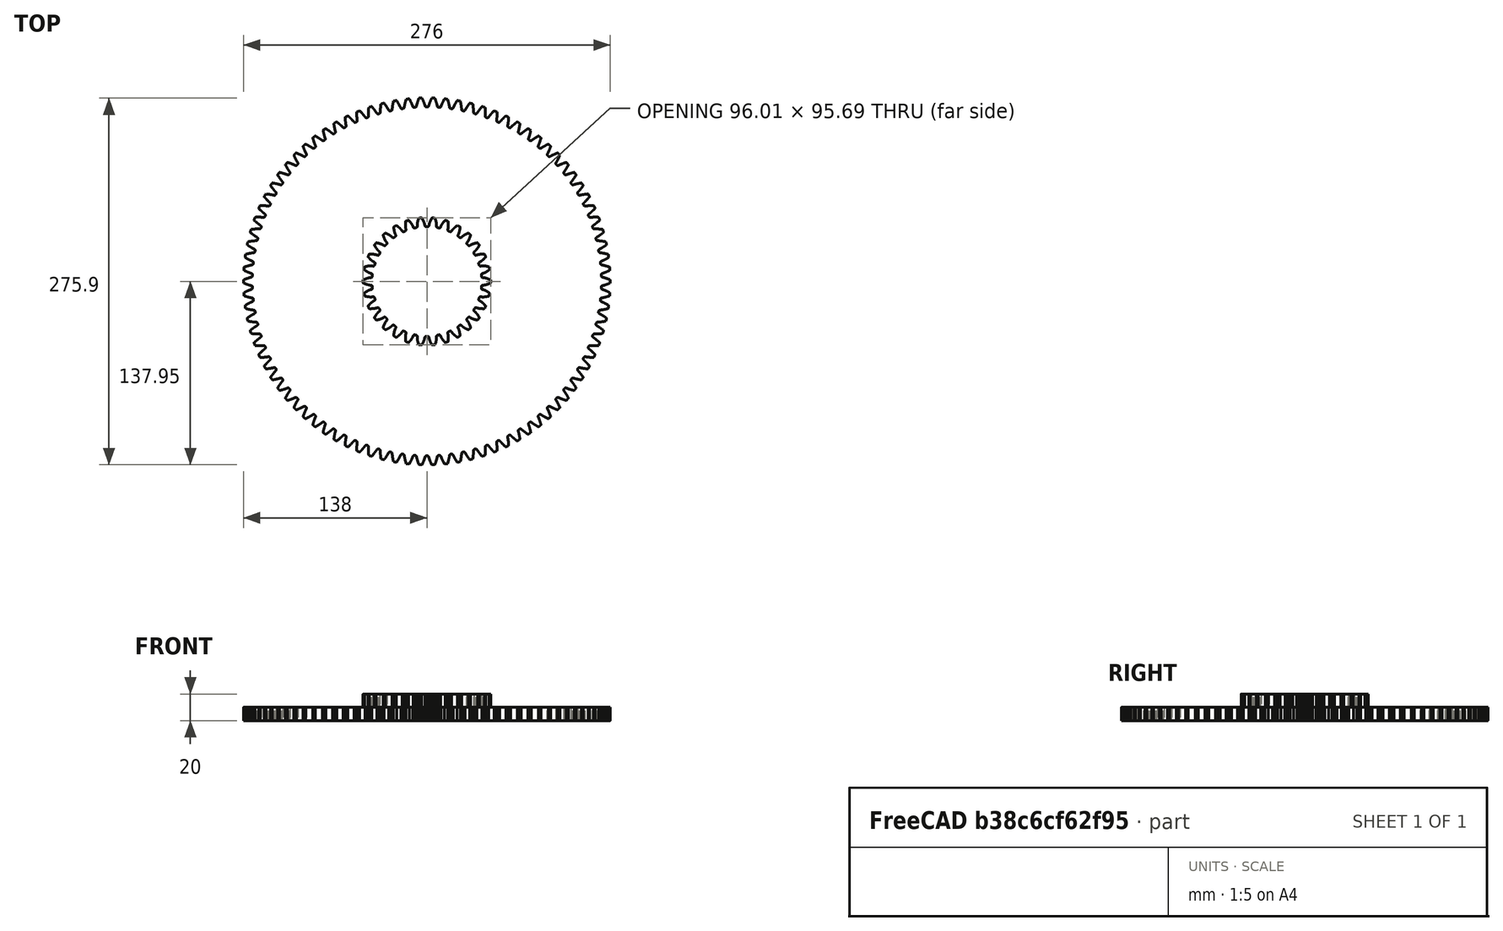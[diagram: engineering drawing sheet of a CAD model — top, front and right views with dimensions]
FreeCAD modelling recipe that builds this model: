
FCSTD DOCUMENT  (FreeCAD 0.20R29177 +426 (Git))
Label: involute-panet
License: All rights reserved
LicenseURL: http://en.wikipedia.org/wiki/All_rights_reserved
objects: Part::Part2DObjectPython×2, PartDesign::Body×2, PartDesign::Pad×2
note: 8 computed .brp shape members not serialized (recipe doc carries the construction recipe); baked Part::Feature solids carry a one-line shape summary decoded from their .brp

FEATURE [Part::Part2DObjectPython] InvoluteGear  # Draft 2D object (typed FeaturePython)
  ExternalGear = true
  HighPrecision = true
  Modules = 3
  NumberOfTeeth = 30
  PressureAngle = 20
FEATURE [PartDesign::Body] Body001
  Origin = -> Origin001
FEATURE [PartDesign::Pad] Pad
  Direction = (0,0,1)
  Length = 20
  Length2 = 10
  Profile = -> InvoluteGear
  ReferenceAxis = -> InvoluteGear [N_Axis]
  Type = 0
FEATURE [Part::Part2DObjectPython] InvoluteGear001  # Draft 2D object (typed FeaturePython)
  ExternalGear = true
  HighPrecision = true
  Modules = 3
  NumberOfTeeth = 90
  PressureAngle = 20
FEATURE [PartDesign::Pad] Pad001
  BaseFeature = -> Pad
  Direction = (0,0,1)
  Length = 10
  Length2 = 10
  Profile = -> InvoluteGear001
  ReferenceAxis = -> InvoluteGear001 [N_Axis]
  Type = 0
FEATURE [PartDesign::Body] Body
  Group = -> [InvoluteGear,Pad,InvoluteGear001,Pad001]
  Origin = -> Origin
  Tip = -> Pad001
